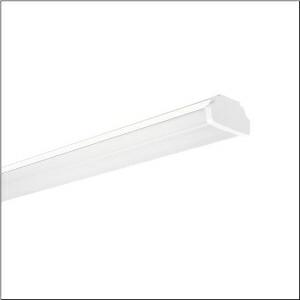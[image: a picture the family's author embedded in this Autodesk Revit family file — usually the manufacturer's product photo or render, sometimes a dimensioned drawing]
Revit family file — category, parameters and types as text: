
# Revit family: modario_r__31_gen_2_53bm812cv6a5d2_682d
name_source: partatom
category: Lighting Fixtures
units: mm (PartAtom-declared; Revit-internal decimal feet)

## family parameters
Cut with Voids When Loaded = No
Host = Face
Light Source = No
Part Type = Normal
Room Calculation Point = No
Round Connector Dimension = Use Diameter
Shared = No

## types (1)
- --- (1 x LED, 10550 lm, 56.5 W, 6500K)
    Apparent Load = 57 VA
    CIE Flux Codes = 47 80 95 93 100
    Color Rendering = 80
    Color Temperature = 6500K
    Default Elevation = 1800 mm
    Description = Modario® 31 Gen.2, luminaire insert, of sheet steel, coil coated, white, length: 1.495mm, width: 81mm, height: 82mm, 5x system unit, system units: 299mm, LED rated luminous flux: 10.550lm, light colour: 865, control gear: ON/OFF Multilumen, CLOi, with plug, 3-pole, with phase selection, mains connection: 220..240V, AC, 50/60Hz, start of lifetime: 57W, end of service life: 68W, through-wiring accessed according to module size, primary optical cover: cover, of PMMA, light emission: direct distribution, primary light characteristic: symmetric, protection rating (complete): IP20, protection rating (LED compartment): IP50, insulation class (complete): insulation class I (protective earthing), certification: CE, ENEC, VDE, UKCA, impact resistance: IK03, permissible ambient temperature for indoor applications: -35..+40°C, corresponds to IFS (International Featured Standards) requirements for safety and quality in the food industry, reducing of maximum allowable ambient temperature of 5°C with ceiling mounting, IP40 when using the optional accessory 5TP9018, packaging unit: 1 piece
    Height = 92 mm
    Lamp = 1 x LED
    Lamp Light Flux = 10550 lm
    Lamp Power = 56.5 W
    Lamp count = 1
    Length = 1495 mm
    Luminous efficacy = 187 lm/W
    Manufacturer = Siteco
    ModVariant = No
    Model = 53BM812CV6A5D2
    Mounting Place = Ceiling
    Mounting Type = Pendant
    Number of Poles = 1
    OnlyDefault = Yes
    Power Factor = 1
    Product Name = Modario® 31 Gen.2
    Product group = luminaire insert | ceiling pendant
    ProductGroupID = 902
    Protection Class = Protection class I
    Protection Degree = IP 20
    RLX_Detail_Level = 1
    RLX_Emergency_Light_Flux = 0 lm
    RLX_Emergency_Type = 0
    RLX_Emergency_Type_DB = No
    RlxData = <blob elided: 40057 chars, md5=bdd5cba5>
    Socket = socket
    Standby Power = 0 W
    System Light Flux = 10550 lm
    System Power = 57 W
    Type Comments = factory setting: luminous flux: 100 % | (A | C | E) | 133 mA
    Type Image = l_1341886.jpg
    URL = http://relux.com
    VarID = @adj_054105
    Voltage = 0 V
    Weight = 0.00 kg
    Width = 81 mm

## geometry (parser evidence)
native form markers: Blend x4, Sweep x12
no freeform markers — native parametric forms only
